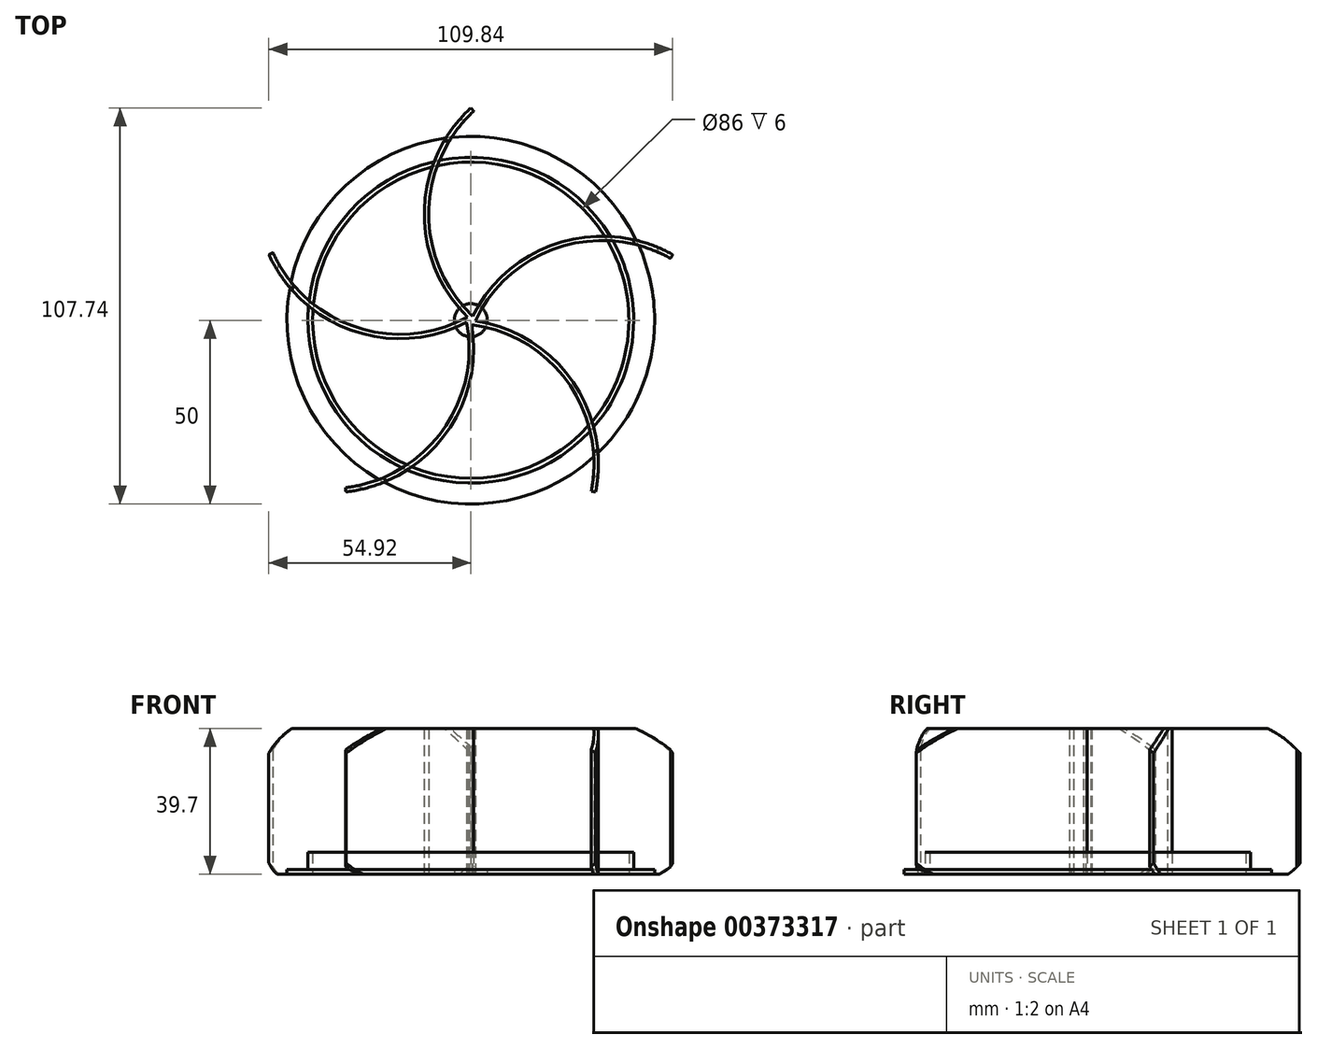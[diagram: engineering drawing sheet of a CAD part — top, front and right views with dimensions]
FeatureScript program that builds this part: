
annotation { "Feature Type Name" : "Feature", "Feature Type Description" : "" }
export const myFeature = defineFeature(function(context is Context, id is Id, definition is map)
    precondition{}
    {
        {
            var Q0;
            Q0=qCreatedBy(makeId("Top.planeOp"),FACE);
            var sketch = newSketch(context, id + "F0", { "sketchPlane" : qUnion([Q0])});
            skCircle(sketch, "E0", {"center": v(0, 0) * mm, "radius": 50 * mm});
            skCircle(sketch, "E1.0", {"center": v(0, 0) * mm, "radius": 43 * mm});
            skCircle(sketch, "E2.0", {"center": v(0, 0) * mm, "radius": 44.3 * mm});
            skCircle(sketch, "E3", {"center": v(0, 0) * mm, "radius": 4.5 * mm});
            skSolve(sketch);
        }
        {
            var Q0;
            Q0=makeQuery(id+"F0.imprint","IMPRINT",FACE,{"disambiguationData":[TD([[makeQuery(id+"F0.imprint","IMPRINT",EDGE,{"derivedFrom":sQuery(id+"F0.wireOp",EDGE,"E1.0")}),-1.0]])]});
            extrude(context, id + "F1", {"entities" : qUnion([Q0]), "depth" : 6 * mm});
        }
        {
            var Q0;
            Q0=makeQuery(id+"F0.imprint","IMPRINT",FACE,{"disambiguationData":[TD([[makeQuery(id+"F0.imprint","IMPRINT",EDGE,{"derivedFrom":sQuery(id+"F0.wireOp",EDGE,"E0")}),1.0]])]});
            var Q1;
            Q1=makeQuery(id+"F0.imprint","IMPRINT",FACE,{"disambiguationData":[TD([[makeQuery(id+"F0.imprint","IMPRINT",EDGE,{"derivedFrom":sQuery(id+"F0.wireOp",EDGE,"E3")}),1.0]])]});
            extrude(context, id + "F2", {"entities" : qUnion([Q0, Q1]), "operationType" : NewBodyOperationType.ADD, "depth" : 1.3 * mm});
        }
        {
            var Q0;
            Q0=qCreatedBy(makeId("Top.planeOp"),FACE);
            var sketch = newSketch(context, id + "F3", { "sketchPlane" : qUnion([Q0])});
            skArc(sketch, "E4", {"start": v(0, 57.74) * mm, "mid": v(-12.64, 28.87) * mm, "end": v(0, 0) * mm});
            skArc(sketch, "E5.0", {"start": v(0.81, 56.86) * mm, "mid": v(-11.44, 28.87) * mm, "end": v(0.81, 0.88) * mm});
            skLineSegment(sketch, "E6", {"start": v(0.81, 56.86) * mm, "end": v(0, 57.74) * mm});
            skLineSegment(sketch, "E7", {"start": v(0.81, 0.88) * mm, "end": v(0, 0) * mm});
            skArc(sketch, "E8.1.0", {"start": v(-54.92, 17.84) * mm, "mid": v(-31.37, -3.1) * mm, "end": v(0, 0) * mm});
            skLineSegment(sketch, "E8.1.1", {"start": v(-53.83, 18.35) * mm, "end": v(-54.92, 17.84) * mm});
            skArc(sketch, "E8.1.2", {"start": v(-53.83, 18.35) * mm, "mid": v(-31, -1.96) * mm, "end": v(-0.59, 1.05) * mm});
            skLineSegment(sketch, "E8.1.3", {"start": v(-0.59, 1.05) * mm, "end": v(0, 0) * mm});
            skArc(sketch, "E8.2.0", {"start": v(-33.94, -46.72) * mm, "mid": v(-6.74, -30.79) * mm, "end": v(0, 0) * mm});
            skLineSegment(sketch, "E8.2.1", {"start": v(-34.08, -45.52) * mm, "end": v(-33.94, -46.72) * mm});
            skArc(sketch, "E8.2.2", {"start": v(-34.08, -45.52) * mm, "mid": v(-7.71, -30.08) * mm, "end": v(-1.18, -0.23) * mm});
            skLineSegment(sketch, "E8.2.3", {"start": v(-1.18, -0.23) * mm, "end": v(0, 0) * mm});
            skArc(sketch, "E8.3.0", {"start": v(33.94, -46.72) * mm, "mid": v(27.2, -15.93) * mm, "end": v(0, 0) * mm});
            skLineSegment(sketch, "E8.3.1", {"start": v(32.76, -46.48) * mm, "end": v(33.94, -46.72) * mm});
            skArc(sketch, "E8.3.2", {"start": v(32.76, -46.48) * mm, "mid": v(26.23, -16.63) * mm, "end": v(-0.14, -1.2) * mm});
            skLineSegment(sketch, "E8.3.3", {"start": v(-0.14, -1.2) * mm, "end": v(0, 0) * mm});
            skArc(sketch, "E8.4.0", {"start": v(54.92, 17.84) * mm, "mid": v(23.55, 20.95) * mm, "end": v(0, 0) * mm});
            skLineSegment(sketch, "E8.4.1", {"start": v(54.33, 16.8) * mm, "end": v(54.92, 17.84) * mm});
            skArc(sketch, "E8.4.2", {"start": v(54.33, 16.8) * mm, "mid": v(23.92, 19.8) * mm, "end": v(1.1, -0.5) * mm});
            skLineSegment(sketch, "E8.4.3", {"start": v(1.1, -0.5) * mm, "end": v(0, 0) * mm});
            skPoint(sketch, "E8.center", {"position": v(0, 0) * mm});
            skSolve(sketch);
        }
        {
            var Q0;
            Q0 = qSketchRegion(id + "F3", true);
            extrude(context, id + "F4", {"entities" : qUnion([Q0]), "depth" : 39.7 * mm});
        }
        {
            var Q0;
            Q0=qCreatedBy(makeId("Right.planeOp"),FACE);
            var sketch = newSketch(context, id + "F5", { "sketchPlane" : qUnion([Q0])});
            skLineSegment(sketch, "E9", {"start": v(33.5, 43.74) * mm, "end": v(64.44, 43.74) * mm});
            skLineSegment(sketch, "E10", {"start": v(64.44, 43.74) * mm, "end": v(64.44, 21.3) * mm});
            skArc(sketch, "E11", {"start": v(64.44, 21.3) * mm, "mid": v(52.6, 37.54) * mm, "end": v(33.5, 43.74) * mm});
            skLineSegment(sketch, "E12", {"start": v(48.3, -2.6) * mm, "end": v(61.47, -2.6) * mm});
            skLineSegment(sketch, "E13", {"start": v(61.47, -2.6) * mm, "end": v(61.47, 13.42) * mm});
            skArc(sketch, "E14", {"start": v(48.3, -2.6) * mm, "mid": v(57.76, 3.06) * mm, "end": v(61.47, 13.42) * mm});
            skSolve(sketch);
        }
        {
            var Q0;
            Q0 = qSketchRegion(id + "F5", true);
            var Q1;
            Q1=makeQuery(id+"F1.opExtrude","SWEPT_FACE",FACE,{"disambiguationData":[OSD([sQuery(id+"F0.wireOp",EDGE,"E2.0")])]});
            revolve(context, id + "F6", {"operationType" : NewBodyOperationType.REMOVE, "entities" : qUnion([Q0]), "axis" : qUnion([Q1]), "revolveType" : RevolveType.FULL, "oppositeDirection" : true});
        }
    });
